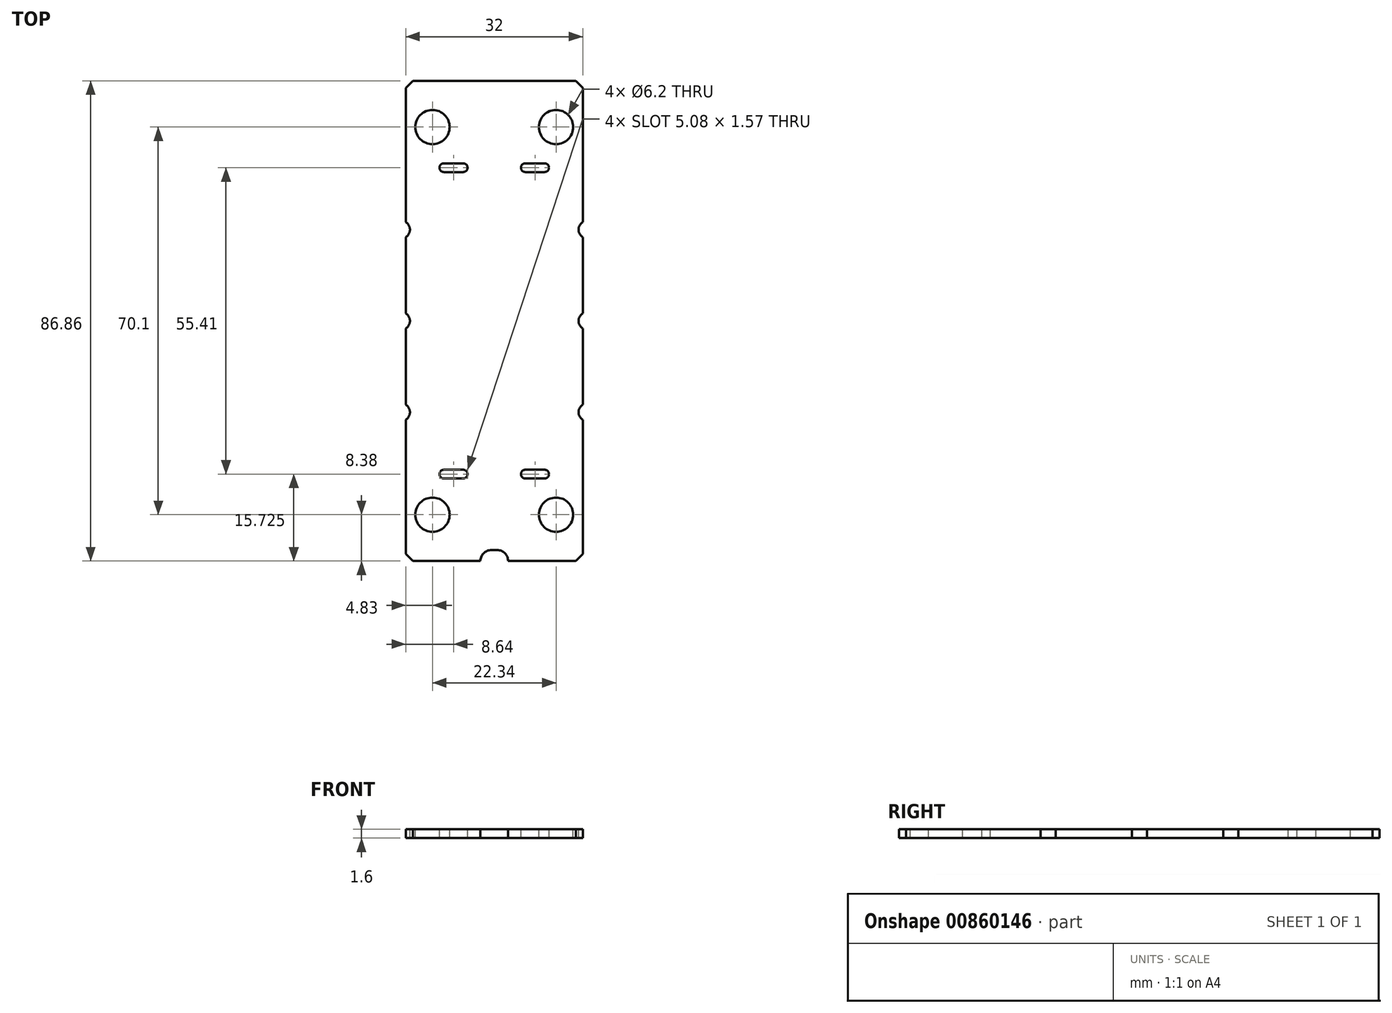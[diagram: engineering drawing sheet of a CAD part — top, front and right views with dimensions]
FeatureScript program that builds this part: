
annotation { "Feature Type Name" : "Feature", "Feature Type Description" : "" }
export const myFeature = defineFeature(function(context is Context, id is Id, definition is map)
    precondition{}
    {
        {
            var Q0;
            Q0=qCreatedBy(makeId("Top.planeOp"),FACE);
            var sketch = newSketch(context, id + "F0", { "sketchPlane" : qUnion([Q0])});
            skLineSegment(sketch, "E0.bottom", {"start": v(-16, 43.43) * mm, "end": v(16, 43.43) * mm});
            skLineSegment(sketch, "E0.top", {"start": v(-16, -43.43) * mm, "end": v(16, -43.43) * mm});
            skLineSegment(sketch, "E0.left", {"start": v(-16, 43.43) * mm, "end": v(-16, -43.43) * mm});
            skLineSegment(sketch, "E0.right", {"start": v(16, 43.43) * mm, "end": v(16, -43.43) * mm});
            skSolve(sketch);
        }
        {
            var Q0;
            Q0=makeQuery(id+"F0.imprint","IMPRINT",FACE,{"disambiguationData":[TD([[makeQuery(id+"F0.imprint","IMPRINT",EDGE,{"derivedFrom":sQuery(id+"F0.wireOp",EDGE,"E0.bottom")}),-1.0]])]});
            extrude(context, id + "F1", {"entities" : qUnion([Q0]), "depth" : 1.6 * mm, "offsetDistance" : 25 * mm});
        }
        {
            var Q0;
            Q0=makeQuery(id+"F1.opExtrude","CAP_FACE",FACE,{"disambiguationData":[OSD([sQuery(id+"F0.wireOp",EDGE,"E0.bottom"),sQuery(id+"F0.wireOp",EDGE,"E0.top"),sQuery(id+"F0.wireOp",EDGE,"E0.left"),sQuery(id+"F0.wireOp",EDGE,"E0.right")])],"isStart":false});
            var sketch = newSketch(context, id + "F2", { "sketchPlane" : qUnion([Q0])});
            skCircle(sketch, "E1", {"center": v(-11.17, 35.05) * mm, "radius": 3.1 * mm});
            skCircle(sketch, "E2", {"center": v(11.17, 35.05) * mm, "radius": 3.1 * mm});
            skCircle(sketch, "E3", {"center": v(-11.17, -35.05) * mm, "radius": 3.1 * mm});
            skCircle(sketch, "E4", {"center": v(11.17, -35.05) * mm, "radius": 3.1 * mm});
            skLineSegment(sketch, "E5.bottom", {"start": v(5.6, 28.5) * mm, "end": v(9.12, 28.5) * mm});
            skLineSegment(sketch, "E5.top", {"start": v(5.6, 26.92) * mm, "end": v(9.12, 26.92) * mm});
            skLineSegment(sketch, "E5.left", {"start": v(4.82, 27.7) * mm, "end": v(4.82, 27.7) * mm});
            skLineSegment(sketch, "E5.right", {"start": v(9.9, 27.7) * mm, "end": v(9.9, 27.7) * mm});
            skLineSegment(sketch, "E6.bottom", {"start": v(-9.12, 28.5) * mm, "end": v(-5.6, 28.5) * mm});
            skLineSegment(sketch, "E6.top", {"start": v(-9.12, 26.92) * mm, "end": v(-5.6, 26.92) * mm});
            skLineSegment(sketch, "E6.left", {"start": v(-9.9, 27.7) * mm, "end": v(-9.9, 27.7) * mm});
            skLineSegment(sketch, "E6.right", {"start": v(-4.82, 27.7) * mm, "end": v(-4.82, 27.7) * mm});
            skCircle(sketch, "E7", {"center": v(16.82, 16.51) * mm, "radius": 1.58 * mm});
            skCircle(sketch, "E8", {"center": v(16.82, 0) * mm, "radius": 1.58 * mm});
            skPoint(sketch, "E8.centerSnap0", {"position": v(16, 0) * mm});
            skCircle(sketch, "E9", {"center": v(16.82, -16.51) * mm, "radius": 1.58 * mm});
            skCircle(sketch, "E10", {"center": v(-16.82, 0) * mm, "radius": 1.58 * mm});
            skCircle(sketch, "E11", {"center": v(-16.82, 16.51) * mm, "radius": 1.58 * mm});
            skCircle(sketch, "E12", {"center": v(-16.82, -16.51) * mm, "radius": 1.58 * mm});
            skPoint(sketch, "E13.visualSharp", {"position": v(-9.9, 28.5) * mm});
            skArc(sketch, "E13.filletArc", {"start": v(-9.12, 28.5) * mm, "mid": v(-9.67, 28.26) * mm, "end": v(-9.9, 27.7) * mm});
            skPoint(sketch, "E14.visualSharp", {"position": v(-9.9, 26.92) * mm});
            skArc(sketch, "E14.filletArc", {"start": v(-9.9, 27.7) * mm, "mid": v(-9.67, 27.15) * mm, "end": v(-9.12, 26.92) * mm});
            skPoint(sketch, "E15.visualSharp", {"position": v(-4.82, 26.92) * mm});
            skArc(sketch, "E15.filletArc", {"start": v(-5.6, 26.92) * mm, "mid": v(-5.05, 27.15) * mm, "end": v(-4.82, 27.7) * mm});
            skPoint(sketch, "E16.visualSharp", {"position": v(-4.82, 28.5) * mm});
            skArc(sketch, "E16.filletArc", {"start": v(-4.82, 27.7) * mm, "mid": v(-5.05, 28.26) * mm, "end": v(-5.6, 28.5) * mm});
            skPoint(sketch, "E17.visualSharp", {"position": v(4.82, 28.5) * mm});
            skArc(sketch, "E17.filletArc", {"start": v(5.6, 28.5) * mm, "mid": v(5.05, 28.26) * mm, "end": v(4.82, 27.7) * mm});
            skPoint(sketch, "E18.visualSharp", {"position": v(4.82, 26.92) * mm});
            skArc(sketch, "E18.filletArc", {"start": v(4.82, 27.7) * mm, "mid": v(5.05, 27.15) * mm, "end": v(5.6, 26.92) * mm});
            skPoint(sketch, "E19.visualSharp", {"position": v(9.9, 26.92) * mm});
            skArc(sketch, "E19.filletArc", {"start": v(9.12, 26.92) * mm, "mid": v(9.67, 27.15) * mm, "end": v(9.9, 27.7) * mm});
            skPoint(sketch, "E20.visualSharp", {"position": v(9.9, 28.5) * mm});
            skArc(sketch, "E20.filletArc", {"start": v(9.9, 27.7) * mm, "mid": v(9.67, 28.26) * mm, "end": v(9.12, 28.5) * mm});
            skLineSegment(sketch, "E21.bottom", {"start": v(-9.12, -26.92) * mm, "end": v(-5.6, -26.92) * mm});
            skLineSegment(sketch, "E21.top", {"start": v(-9.12, -28.5) * mm, "end": v(-5.6, -28.5) * mm});
            skLineSegment(sketch, "E21.left", {"start": v(-9.9, -27.7) * mm, "end": v(-9.9, -27.7) * mm});
            skLineSegment(sketch, "E21.right", {"start": v(-4.82, -27.7) * mm, "end": v(-4.82, -27.7) * mm});
            skLineSegment(sketch, "E22.bottom", {"start": v(5.6, -26.92) * mm, "end": v(9.12, -26.92) * mm});
            skLineSegment(sketch, "E22.top", {"start": v(5.6, -28.5) * mm, "end": v(9.12, -28.5) * mm});
            skLineSegment(sketch, "E22.left", {"start": v(4.82, -27.7) * mm, "end": v(4.82, -27.7) * mm});
            skLineSegment(sketch, "E22.right", {"start": v(9.9, -27.7) * mm, "end": v(9.9, -27.7) * mm});
            skPoint(sketch, "E23.visualSharp", {"position": v(-9.9, -28.5) * mm});
            skArc(sketch, "E23.filletArc", {"start": v(-9.9, -27.7) * mm, "mid": v(-9.67, -28.26) * mm, "end": v(-9.12, -28.5) * mm});
            skPoint(sketch, "E24.visualSharp", {"position": v(-9.9, -26.92) * mm});
            skArc(sketch, "E24.filletArc", {"start": v(-9.12, -26.92) * mm, "mid": v(-9.67, -27.15) * mm, "end": v(-9.9, -27.7) * mm});
            skPoint(sketch, "E25.visualSharp", {"position": v(-4.82, -28.5) * mm});
            skArc(sketch, "E25.filletArc", {"start": v(-5.6, -28.5) * mm, "mid": v(-5.05, -28.26) * mm, "end": v(-4.82, -27.7) * mm});
            skPoint(sketch, "E26.visualSharp", {"position": v(-4.82, -26.92) * mm});
            skArc(sketch, "E26.filletArc", {"start": v(-4.82, -27.7) * mm, "mid": v(-5.05, -27.15) * mm, "end": v(-5.6, -26.92) * mm});
            skPoint(sketch, "E27.visualSharp", {"position": v(4.82, -26.92) * mm});
            skArc(sketch, "E27.filletArc", {"start": v(5.6, -26.92) * mm, "mid": v(5.05, -27.15) * mm, "end": v(4.82, -27.7) * mm});
            skPoint(sketch, "E28.visualSharp", {"position": v(4.82, -28.5) * mm});
            skArc(sketch, "E28.filletArc", {"start": v(4.82, -27.7) * mm, "mid": v(5.05, -28.26) * mm, "end": v(5.6, -28.5) * mm});
            skPoint(sketch, "E29.visualSharp", {"position": v(9.9, -28.5) * mm});
            skArc(sketch, "E29.filletArc", {"start": v(9.12, -28.5) * mm, "mid": v(9.67, -28.26) * mm, "end": v(9.9, -27.7) * mm});
            skPoint(sketch, "E30.visualSharp", {"position": v(9.9, -26.92) * mm});
            skArc(sketch, "E30.filletArc", {"start": v(9.9, -27.7) * mm, "mid": v(9.67, -27.15) * mm, "end": v(9.12, -26.92) * mm});
            skLineSegment(sketch, "E31.bottom", {"start": v(-2.5, -41.43) * mm, "end": v(2.5, -41.43) * mm});
            skLineSegment(sketch, "E31.top", {"start": v(-2.5, -43.9) * mm, "end": v(2.5, -43.9) * mm});
            skLineSegment(sketch, "E31.left", {"start": v(-2.5, -41.43) * mm, "end": v(-2.5, -43.9) * mm});
            skLineSegment(sketch, "E31.right", {"start": v(2.5, -41.43) * mm, "end": v(2.5, -43.9) * mm});
            skSolve(sketch);
        }
        {
            var Q0;
            Q0 = qSketchRegion(id + "F2", true);
            extrude(context, id + "F3", {"entities" : qUnion([Q0]), "operationType" : NewBodyOperationType.REMOVE, "oppositeDirection" : true, "depth" : 25 * mm, "offsetDistance" : 25 * mm});
        }
        {
            var Q0;
            Q0=makeQuery(id+"F1.opExtrude","SWEPT_EDGE",EDGE,{"disambiguationData":[OSD([sQuery(id+"F0.wireOp",EDGE,"E0.bottom"),sQuery(id+"F0.wireOp",EDGE,"E0.right")])]});
            var Q1;
            Q1=makeQuery(id+"F1.opExtrude","SWEPT_EDGE",EDGE,{"disambiguationData":[OSD([sQuery(id+"F0.wireOp",EDGE,"E0.bottom"),sQuery(id+"F0.wireOp",EDGE,"E0.left")])]});
            var Q2;
            Q2=makeQuery(id+"F1.opExtrude","SWEPT_EDGE",EDGE,{"disambiguationData":[OSD([sQuery(id+"F0.wireOp",EDGE,"E0.top"),sQuery(id+"F0.wireOp",EDGE,"E0.right")])]});
            var Q3;
            Q3=makeQuery(id+"F1.opExtrude","SWEPT_EDGE",EDGE,{"disambiguationData":[OSD([sQuery(id+"F0.wireOp",EDGE,"E0.top"),sQuery(id+"F0.wireOp",EDGE,"E0.left")])]});
            chamfer(context, id + "F4", {"entities" : qUnion([Q0, Q1, Q2, Q3]), "width" : 1.27 * mm, "tangentPropagation" : true});
        }
        {
            var Q0;
            Q0=makeQuery(id+"F3.boolean.opBoolean","COPY",EDGE,{"derivedFrom":makeQuery(id+"F3.opExtrude","SWEPT_EDGE",EDGE,{"disambiguationData":[OSD([sQuery(id+"F2.wireOp",EDGE,"E31.bottom"),sQuery(id+"F2.wireOp",EDGE,"E31.left")])]})});
            var Q1;
            Q1=makeQuery(id+"F3.boolean.opBoolean","COPY",EDGE,{"derivedFrom":makeQuery(id+"F3.opExtrude","SWEPT_EDGE",EDGE,{"disambiguationData":[OSD([sQuery(id+"F2.wireOp",EDGE,"E31.bottom"),sQuery(id+"F2.wireOp",EDGE,"E31.right")])]})});
            fillet(context, id + "F5", {"entities" : qUnion([Q0, Q1]), "radius" : 2 * mm, "tangentPropagation" : true, "allowEdgeOverflow" : false});
        }
    });
